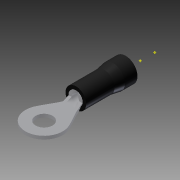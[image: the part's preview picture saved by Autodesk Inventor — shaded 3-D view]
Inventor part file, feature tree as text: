
AUTODESK INVENTOR PART (.ipt)
format: ipt  version: 2011 (Build 150239000, 239)  size: 171,008 bytes
history: native  units: mm
features: other x4, plane x2, imported_body x1, sketch x1
ambient origin geometry x8: Origin, YZ Plane, XZ Plane, XY Plane, X Axis, Y Axis, Z Axis, Center Point
bodies: Solid1 (feature_tree)
feature tree (8):
  imported_body  "Base1"
  sketch  "Sketch1"  dims[d0=3.175mm d1=6.35mm]
  other  "Work Point2"
  other  "Work Point3"
  plane  "Work Plane1"
  other  "Work Axis1"
  plane  "Work Plane2"
  other  "Work Axis2"
